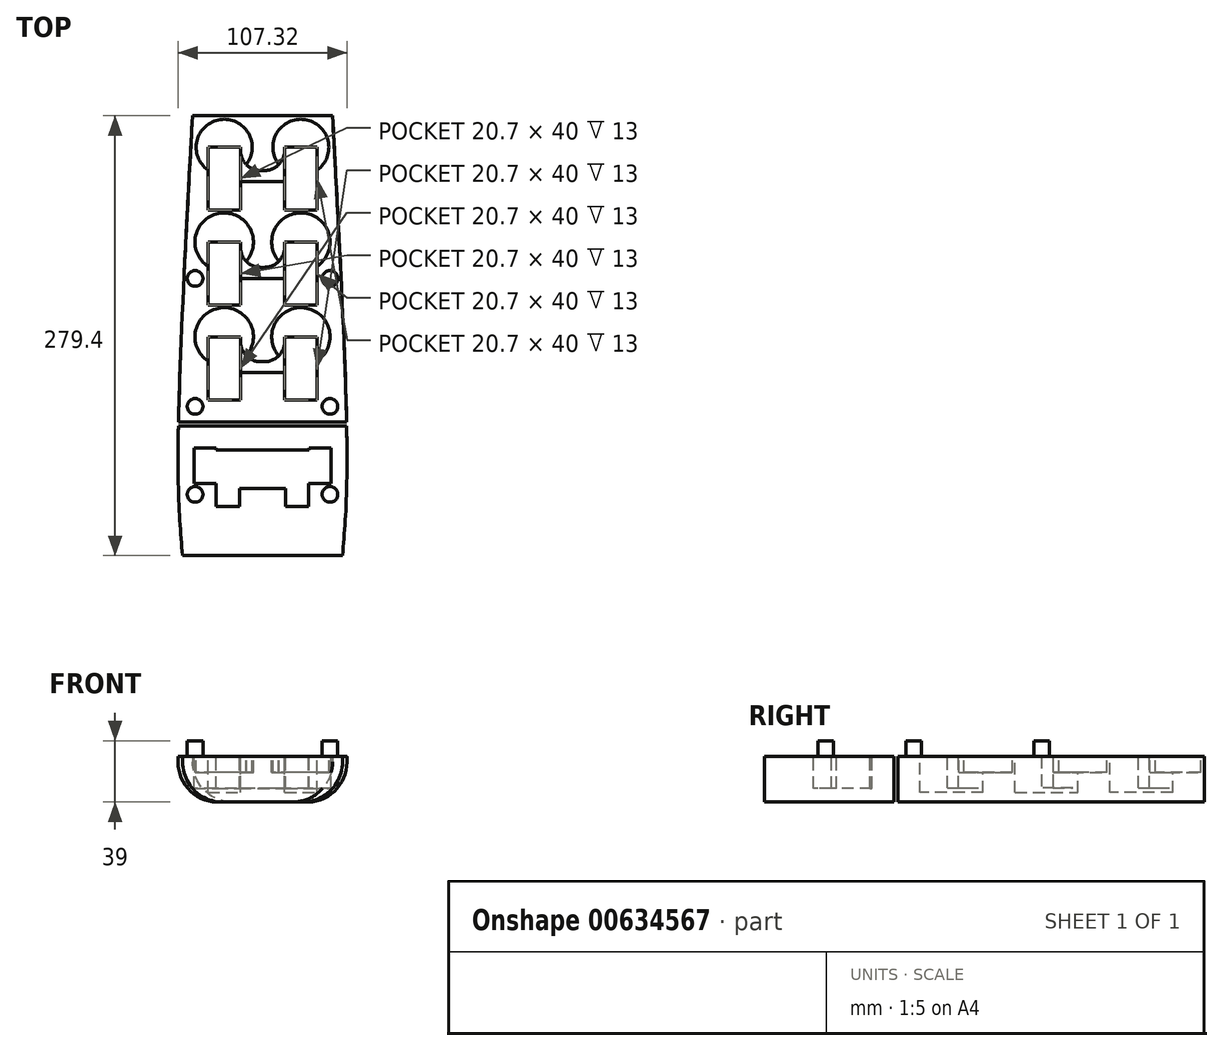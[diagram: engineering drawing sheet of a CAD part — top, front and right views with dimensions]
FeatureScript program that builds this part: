
annotation { "Feature Type Name" : "Feature", "Feature Type Description" : "" }
export const myFeature = defineFeature(function(context is Context, id is Id, definition is map)
    precondition{}
    {
        {
            var Q0;
            Q0=qCreatedBy(makeId("Top.planeOp"),FACE);
            var sketch = newSketch(context, id + "F0", { "sketchPlane" : qUnion([Q0])});
            skLineSegment(sketch, "E0", {"start": v(-44.45, 139.7) * mm, "end": v(44.45, 139.7) * mm});
            skLineSegment(sketch, "E1", {"start": v(0, 139.7) * mm, "end": v(0, -139.7) * mm, "construction": true});
            skLineSegment(sketch, "E2", {"start": v(0, -139.7) * mm, "end": v(-50.8, -139.7) * mm});
            skFitSpline(sketch, "E3", {"points": [v(-44.45, 139.7) * mm, v(-53.65, -82.07) * mm, v(-50.8, -139.7) * mm], "startDerivative": vector(-21.3, -389.22) * mm, "endDerivative": vector(12.22, -142.93) * mm});
            skFitSpline(sketch, "E4.MirrorCS", {"points": [v(44.45, 139.7) * mm, v(53.65, -82.07) * mm, v(50.8, -139.7) * mm], "startDerivative": vector(21.3, -389.22) * mm, "endDerivative": vector(-12.22, -142.93) * mm});
            skLineSegment(sketch, "E5.MirrorCS", {"start": v(0, -139.7) * mm, "end": v(50.8, -139.7) * mm});
            skSolve(sketch);
        }
        {
            var Q0;
            Q0=qSketchRegion(id+"F0",true);
            extrude(context, id + "F1", {"entities" : qUnion([Q0]), "depth" : 29 * mm, "offsetDistance" : 25.4 * mm});
        }
        {
            var Q0;
            Q0=makeQuery(id+"F1.opExtrude","CAP_EDGE",EDGE,{"disambiguationData":[OSD([sQuery(id+"F0.wireOp",EDGE,"E3")])],"isStart":true});
            var Q1;
            Q1=makeQuery(id+"F1.opExtrude","CAP_EDGE",EDGE,{"disambiguationData":[OSD([sQuery(id+"F0.wireOp",EDGE,"E4.MirrorCS")])],"isStart":true});
            fillet(context, id + "F2", {"entities" : qUnion([Q0, Q1]), "radius" : 25.4 * mm, "tangentPropagation" : true, "allowEdgeOverflow" : false});
        }
        {
            var Q0;
            Q0=makeQuery(id+"F1.opExtrude","CAP_FACE",FACE,{"disambiguationData":[OSD([sQuery(id+"F0.wireOp",EDGE,"E0"),sQuery(id+"F0.wireOp",EDGE,"E2"),sQuery(id+"F0.wireOp",EDGE,"E3"),sQuery(id+"F0.wireOp",EDGE,"E4.MirrorCS"),sQuery(id+"F0.wireOp",EDGE,"E5.MirrorCS")])],"isStart":false});
            var sketch = newSketch(context, id + "F3", { "sketchPlane" : qUnion([Q0])});
            skLineSegment(sketch, "E6.bottom", {"start": v(-34.7, 119.7) * mm, "end": v(-14, 119.7) * mm});
            skLineSegment(sketch, "E6.top", {"start": v(-34.7, 79.7) * mm, "end": v(-14, 79.7) * mm});
            skLineSegment(sketch, "E6.left", {"start": v(-34.7, 119.7) * mm, "end": v(-34.7, 79.7) * mm});
            skLineSegment(sketch, "E6.right", {"start": v(-14, 119.7) * mm, "end": v(-14, 79.7) * mm});
            skLineSegment(sketch, "E7", {"start": v(0, 139.7) * mm, "end": v(0, 0) * mm, "construction": true});
            skLineSegment(sketch, "E8", {"start": v(-38, 69.6) * mm, "end": v(36.85, 69.6) * mm, "construction": true});
            skLineSegment(sketch, "E9.MirrorCS", {"start": v(34.7, 119.7) * mm, "end": v(34.7, 79.7) * mm});
            skLineSegment(sketch, "E10.MirrorCS", {"start": v(14, 119.7) * mm, "end": v(14, 79.7) * mm});
            skLineSegment(sketch, "E11.MirrorCS", {"start": v(34.7, 79.7) * mm, "end": v(14, 79.7) * mm});
            skLineSegment(sketch, "E12.MirrorCS", {"start": v(34.7, 119.7) * mm, "end": v(14, 119.7) * mm});
            skLineSegment(sketch, "E13.MirrorCS", {"start": v(34.7, 19.5) * mm, "end": v(34.7, 59.5) * mm});
            skLineSegment(sketch, "E14.MirrorCS", {"start": v(-14, 19.5) * mm, "end": v(-14, 59.5) * mm});
            skLineSegment(sketch, "E15.MirrorCS", {"start": v(-34.7, 19.5) * mm, "end": v(-34.7, 59.5) * mm});
            skLineSegment(sketch, "E16.MirrorCS", {"start": v(-34.7, 59.5) * mm, "end": v(-14, 59.5) * mm});
            skLineSegment(sketch, "E17.MirrorCS", {"start": v(14, 19.5) * mm, "end": v(14, 59.5) * mm});
            skLineSegment(sketch, "E18.MirrorCS", {"start": v(34.7, 59.5) * mm, "end": v(14, 59.5) * mm});
            skLineSegment(sketch, "E19", {"start": v(-34.7, 19.5) * mm, "end": v(-14, 19.5) * mm});
            skLineSegment(sketch, "E20", {"start": v(14, 19.5) * mm, "end": v(34.7, 19.5) * mm});
            skLineSegment(sketch, "E21", {"start": v(-32.28, 9.4) * mm, "end": v(34.83, 9.4) * mm, "construction": true});
            skLineSegment(sketch, "E22.MirrorCS", {"start": v(-34.7, -40.7) * mm, "end": v(-14, -40.7) * mm});
            skLineSegment(sketch, "E23.MirrorCS", {"start": v(-34.7, -0.7) * mm, "end": v(-14, -0.7) * mm});
            skLineSegment(sketch, "E24.MirrorCS", {"start": v(34.7, -40.7) * mm, "end": v(14, -40.7) * mm});
            skLineSegment(sketch, "E25.MirrorCS", {"start": v(14, -0.7) * mm, "end": v(34.7, -0.7) * mm});
            skLineSegment(sketch, "E26.MirrorCS", {"start": v(-34.7, -0.7) * mm, "end": v(-34.7, -40.7) * mm});
            skLineSegment(sketch, "E27.MirrorCS", {"start": v(-14, -0.7) * mm, "end": v(-14, -40.7) * mm});
            skLineSegment(sketch, "E28.MirrorCS", {"start": v(34.7, -0.7) * mm, "end": v(34.7, -40.7) * mm});
            skLineSegment(sketch, "E29.MirrorCS", {"start": v(14, -0.7) * mm, "end": v(14, -40.7) * mm});
            skSolve(sketch);
        }
        {
            var Q0;
            Q0=qSketchRegion(id+"F3",true);
            extrude(context, id + "F4", {"entities" : qUnion([Q0]), "operationType" : NewBodyOperationType.REMOVE, "oppositeDirection" : true, "depth" : 23 * mm, "offsetDistance" : 25.4 * mm});
        }
        {
            var Q0;
            Q0=makeQuery(id+"F1.opExtrude","CAP_FACE",FACE,{"disambiguationData":[OSD([sQuery(id+"F0.wireOp",EDGE,"E0"),sQuery(id+"F0.wireOp",EDGE,"E2"),sQuery(id+"F0.wireOp",EDGE,"E3"),sQuery(id+"F0.wireOp",EDGE,"E4.MirrorCS"),sQuery(id+"F0.wireOp",EDGE,"E5.MirrorCS")])],"isStart":false});
            var sketch = newSketch(context, id + "F5", { "sketchPlane" : qUnion([Q0])});
            skCircle(sketch, "E30", {"center": v(-24.35, 119.7) * mm, "radius": 17.78 * mm});
            skCircle(sketch, "E31", {"center": v(24.35, 119.7) * mm, "radius": 17.78 * mm});
            skCircle(sketch, "E32", {"center": v(-24.35, 59.5) * mm, "radius": 18.54 * mm});
            skCircle(sketch, "E33", {"center": v(24.35, 59.5) * mm, "radius": 18.54 * mm});
            skCircle(sketch, "E34", {"center": v(-24.35, -0.7) * mm, "radius": 18.54 * mm});
            skCircle(sketch, "E35", {"center": v(24.35, -0.7) * mm, "radius": 18.54 * mm});
            skSolve(sketch);
        }
        {
            var Q0;
            Q0=qSketchRegion(id+"F5",true);
            extrude(context, id + "F6", {"entities" : qUnion([Q0]), "operationType" : NewBodyOperationType.REMOVE, "oppositeDirection" : true, "depth" : 10 * mm, "offsetDistance" : 25.4 * mm});
        }
        {
            var Q0;
            Q0=makeQuery(id+"F1.opExtrude","CAP_FACE",FACE,{"disambiguationData":[OSD([sQuery(id+"F0.wireOp",EDGE,"E0"),sQuery(id+"F0.wireOp",EDGE,"E2"),sQuery(id+"F0.wireOp",EDGE,"E3"),sQuery(id+"F0.wireOp",EDGE,"E4.MirrorCS"),sQuery(id+"F0.wireOp",EDGE,"E5.MirrorCS")])],"isStart":false});
            var sketch = newSketch(context, id + "F7", { "sketchPlane" : qUnion([Q0])});
            skSolve(sketch);
        }
        {
            var Q0;
            Q0=makeQuery(id+"F7.imprint","IMPRINT",FACE,{"disambiguationData":[TD([[makeQuery(id+"F7.imprint","IMPRINT",EDGE,{"derivedFrom":makeQuery(id+"F1.opExtrude","CAP_EDGE",EDGE,{"disambiguationData":[OSD([sQuery(id+"F0.wireOp",EDGE,"E0")])],"isStart":false})}),-1.0]])]});
            var sketch = newSketch(context, id + "F8", { "sketchPlane" : qUnion([Q0])});
            skLineSegment(sketch, "E36.bottom", {"start": v(-22.32, -16.47) * mm, "end": v(25.6, -16.47) * mm});
            skLineSegment(sketch, "E36.top", {"start": v(-22.32, -23.47) * mm, "end": v(25.6, -23.47) * mm});
            skLineSegment(sketch, "E36.left", {"start": v(-22.32, -16.47) * mm, "end": v(-22.32, -23.47) * mm});
            skLineSegment(sketch, "E36.right", {"start": v(25.6, -16.47) * mm, "end": v(25.6, -23.47) * mm});
            skLineSegment(sketch, "E37.bottom", {"start": v(-25.01, 43.48) * mm, "end": v(25.6, 43.48) * mm});
            skLineSegment(sketch, "E37.top", {"start": v(-25.01, 36.48) * mm, "end": v(25.6, 36.48) * mm});
            skLineSegment(sketch, "E37.left", {"start": v(-25.01, 43.48) * mm, "end": v(-25.01, 36.48) * mm});
            skLineSegment(sketch, "E37.right", {"start": v(25.6, 43.48) * mm, "end": v(25.6, 36.48) * mm});
            skLineSegment(sketch, "E38.bottom", {"start": v(-26.09, 104.99) * mm, "end": v(25.6, 104.99) * mm});
            skLineSegment(sketch, "E38.top", {"start": v(-26.09, 97.99) * mm, "end": v(25.6, 97.99) * mm});
            skLineSegment(sketch, "E38.left", {"start": v(-26.09, 104.99) * mm, "end": v(-26.09, 97.99) * mm});
            skLineSegment(sketch, "E38.right", {"start": v(25.6, 104.99) * mm, "end": v(25.6, 97.99) * mm});
            skSolve(sketch);
        }
        {
            var Q0;
            Q0=qSketchRegion(id+"F8",true);
            extrude(context, id + "F9", {"entities" : qUnion([Q0]), "operationType" : NewBodyOperationType.REMOVE, "oppositeDirection" : true, "depth" : 20 * mm, "offsetDistance" : 25.4 * mm});
        }
        {
            var Q0;
            Q0=makeQuery(id+"F9.boolean.opBoolean","INTERSECT",EDGE,{"derivedFrom":[makeQuery(id+"F4.boolean.opBoolean","COPY",FACE,{"derivedFrom":makeQuery(id+"F4.opExtrude","SWEPT_FACE",FACE,{"disambiguationData":[OSD([sQuery(id+"F3.wireOp",EDGE,"E6.right")])]})}),makeQuery(id+"F9.opExtrude","SWEPT_FACE",FACE,{"disambiguationData":[OSD([sQuery(id+"F8.wireOp",EDGE,"E38.bottom")])]})]});
            var Q1;
            Q1=makeQuery(id+"F9.boolean.opBoolean","INTERSECT",EDGE,{"derivedFrom":[makeQuery(id+"F4.boolean.opBoolean","COPY",FACE,{"derivedFrom":makeQuery(id+"F4.opExtrude","SWEPT_FACE",FACE,{"disambiguationData":[OSD([sQuery(id+"F3.wireOp",EDGE,"E10.MirrorCS")])]})}),makeQuery(id+"F9.opExtrude","SWEPT_FACE",FACE,{"disambiguationData":[OSD([sQuery(id+"F8.wireOp",EDGE,"E38.bottom")])]})]});
            var Q2;
            Q2=makeQuery(id+"F9.boolean.opBoolean","INTERSECT",EDGE,{"derivedFrom":[makeQuery(id+"F4.boolean.opBoolean","COPY",FACE,{"derivedFrom":makeQuery(id+"F4.opExtrude","SWEPT_FACE",FACE,{"disambiguationData":[OSD([sQuery(id+"F3.wireOp",EDGE,"E17.MirrorCS")])]})}),makeQuery(id+"F9.opExtrude","SWEPT_FACE",FACE,{"disambiguationData":[OSD([sQuery(id+"F8.wireOp",EDGE,"E37.bottom")])]})]});
            var Q3;
            Q3=makeQuery(id+"F9.boolean.opBoolean","INTERSECT",EDGE,{"derivedFrom":[makeQuery(id+"F4.boolean.opBoolean","COPY",FACE,{"derivedFrom":makeQuery(id+"F4.opExtrude","SWEPT_FACE",FACE,{"disambiguationData":[OSD([sQuery(id+"F3.wireOp",EDGE,"E14.MirrorCS")])]})}),makeQuery(id+"F9.opExtrude","SWEPT_FACE",FACE,{"disambiguationData":[OSD([sQuery(id+"F8.wireOp",EDGE,"E37.bottom")])]})]});
            var Q4;
            Q4=makeQuery(id+"F9.boolean.opBoolean","INTERSECT",EDGE,{"derivedFrom":[makeQuery(id+"F4.boolean.opBoolean","COPY",FACE,{"derivedFrom":makeQuery(id+"F4.opExtrude","SWEPT_FACE",FACE,{"disambiguationData":[OSD([sQuery(id+"F3.wireOp",EDGE,"E27.MirrorCS")])]})}),makeQuery(id+"F9.opExtrude","SWEPT_FACE",FACE,{"disambiguationData":[OSD([sQuery(id+"F8.wireOp",EDGE,"E36.bottom")])]})]});
            var Q5;
            Q5=makeQuery(id+"F9.boolean.opBoolean","INTERSECT",EDGE,{"derivedFrom":[makeQuery(id+"F4.boolean.opBoolean","COPY",FACE,{"derivedFrom":makeQuery(id+"F4.opExtrude","SWEPT_FACE",FACE,{"disambiguationData":[OSD([sQuery(id+"F3.wireOp",EDGE,"E29.MirrorCS")])]})}),makeQuery(id+"F9.opExtrude","SWEPT_FACE",FACE,{"disambiguationData":[OSD([sQuery(id+"F8.wireOp",EDGE,"E36.bottom")])]})]});
            fillet(context, id + "F10", {"entities" : qUnion([Q0, Q1, Q2, Q3, Q4, Q5]), "radius" : 12.7 * mm, "tangentPropagation" : true, "allowEdgeOverflow" : false});
        }
        {
            var Q0;
            Q0=makeQuery(id+"F7.imprint","IMPRINT",FACE,{"disambiguationData":[TD([[makeQuery(id+"F7.imprint","IMPRINT",EDGE,{"derivedFrom":makeQuery(id+"F1.opExtrude","CAP_EDGE",EDGE,{"disambiguationData":[OSD([sQuery(id+"F0.wireOp",EDGE,"E0")])],"isStart":false})}),-1.0]])]});
            var sketch = newSketch(context, id + "F11", { "sketchPlane" : qUnion([Q0])});
            skLineSegment(sketch, "E39.bottom", {"start": v(-65.32, -54.88) * mm, "end": v(72.26, -54.88) * mm});
            skLineSegment(sketch, "E39.top", {"start": v(-65.32, -57.24) * mm, "end": v(72.26, -57.24) * mm});
            skLineSegment(sketch, "E39.left", {"start": v(-65.32, -54.88) * mm, "end": v(-65.32, -57.24) * mm});
            skLineSegment(sketch, "E39.right", {"start": v(72.26, -54.88) * mm, "end": v(72.26, -57.24) * mm});
            skSolve(sketch);
        }
        {
            var Q0;
            Q0=qSketchRegion(id+"F11",true);
            extrude(context, id + "F12", {"entities" : qUnion([Q0]), "operationType" : NewBodyOperationType.REMOVE, "oppositeDirection" : true, "depth" : 508 * mm, "offsetDistance" : 25.4 * mm});
        }
        {
            var Q0;
            Q0=makeQuery(id+"F7.imprint","IMPRINT",FACE,{"disambiguationData":[TD([[makeQuery(id+"F7.imprint","IMPRINT",EDGE,{"derivedFrom":makeQuery(id+"F1.opExtrude","CAP_EDGE",EDGE,{"disambiguationData":[OSD([sQuery(id+"F0.wireOp",EDGE,"E0")])],"isStart":false})}),-1.0]])]});
            var sketch = newSketch(context, id + "F13", { "sketchPlane" : qUnion([Q0])});
            skCircle(sketch, "E40", {"center": v(-42.83, -44.88) * mm, "radius": 4.95 * mm});
            skLineSegment(sketch, "E41", {"start": v(0, 30.1) * mm, "end": v(0, -70.05) * mm, "construction": true});
            skLineSegment(sketch, "E42", {"start": v(-82.32, -4.24) * mm, "end": v(87.3, -4.24) * mm, "construction": true});
            skCircle(sketch, "E43.MirrorC", {"center": v(42.83, -44.88) * mm, "radius": 4.95 * mm});
            skCircle(sketch, "E44.MirrorC", {"center": v(-42.83, 36.4) * mm, "radius": 4.95 * mm});
            skCircle(sketch, "E45.MirrorC", {"center": v(42.83, 36.4) * mm, "radius": 4.95 * mm});
            skLineSegment(sketch, "E46", {"start": v(-86.45, -72.82) * mm, "end": v(91.93, -72.82) * mm, "construction": true});
            skCircle(sketch, "E47.MirrorC", {"center": v(-42.83, -100.76) * mm, "radius": 4.95 * mm});
            skCircle(sketch, "E48.MirrorC", {"center": v(42.83, -100.76) * mm, "radius": 4.95 * mm});
            skSolve(sketch);
        }
        {
            var Q0;
            Q0=qSketchRegion(id+"F13",true);
            extrude(context, id + "F14", {"entities" : qUnion([Q0]), "operationType" : NewBodyOperationType.ADD, "depth" : 10 * mm, "offsetDistance" : 25.4 * mm});
        }
        {
            var Q0;
            Q0=makeQuery(id+"F7.imprint","IMPRINT",FACE,{"disambiguationData":[TD([[makeQuery(id+"F7.imprint","IMPRINT",EDGE,{"derivedFrom":makeQuery(id+"F1.opExtrude","CAP_EDGE",EDGE,{"disambiguationData":[OSD([sQuery(id+"F0.wireOp",EDGE,"E0")])],"isStart":false})}),-1.0]])]});
            var sketch = newSketch(context, id + "F15", { "sketchPlane" : qUnion([Q0])});
            skLineSegment(sketch, "E49", {"start": v(0, 0) * mm, "end": v(0, -126.7) * mm, "construction": true});
            skLineSegment(sketch, "E50", {"start": v(42.6, -57.24) * mm, "end": v(-44.07, -57.24) * mm, "construction": true});
            skLineSegment(sketch, "E51", {"start": v(0, 4.55) * mm, "end": v(0, -51.7) * mm, "construction": true});
            skLineSegment(sketch, "E52.top", {"start": v(-14.62, -97.03) * mm, "end": v(0, -97.03) * mm});
            skLineSegment(sketch, "E52.right", {"start": v(0, -27.56) * mm, "end": v(0, -97.03) * mm});
            skLineSegment(sketch, "E53.bottom", {"start": v(-29.62, -79.23) * mm, "end": v(-14.62, -79.23) * mm});
            skLineSegment(sketch, "E53.top", {"start": v(-29.62, -84.55) * mm, "end": v(-29.48, -84.55) * mm});
            skLineSegment(sketch, "E53.left", {"start": v(-29.62, -79.23) * mm, "end": v(-29.62, -84.55) * mm});
            skLineSegment(sketch, "E53.right", {"start": v(-14.62, -79.23) * mm, "end": v(-14.62, -84.55) * mm});
            skLineSegment(sketch, "E54.bottom", {"start": v(-29.62, -79.23) * mm, "end": v(0, -79.23) * mm});
            skLineSegment(sketch, "E54.top", {"start": v(-29.62, -72.47) * mm, "end": v(0, -72.47) * mm});
            skLineSegment(sketch, "E54.left", {"start": v(-29.62, -79.23) * mm, "end": v(-29.62, -72.47) * mm});
            skLineSegment(sketch, "E54.right", {"start": v(0, -79.23) * mm, "end": v(0, -72.47) * mm});
            skLineSegment(sketch, "E55.bottom", {"start": v(0, -97.03) * mm, "end": v(0, -97.03) * mm});
            skLineSegment(sketch, "E55.top", {"start": v(0, -72.47) * mm, "end": v(0, -72.47) * mm});
            skLineSegment(sketch, "E55.left", {"start": v(0, -97.03) * mm, "end": v(0, -72.47) * mm});
            skLineSegment(sketch, "E55.right", {"start": v(0, -97.03) * mm, "end": v(0, -72.47) * mm});
            skLineSegment(sketch, "E56.bottom", {"start": v(-29.62, -84.55) * mm, "end": v(-43.57, -84.55) * mm});
            skLineSegment(sketch, "E56.top", {"start": v(-29.62, -71.42) * mm, "end": v(-43.57, -71.42) * mm});
            skLineSegment(sketch, "E56.left", {"start": v(-29.62, -84.55) * mm, "end": v(-29.62, -71.42) * mm});
            skLineSegment(sketch, "E56.right", {"start": v(-43.57, -84.55) * mm, "end": v(-43.57, -71.42) * mm});
            skLineSegment(sketch, "E57.MirrorCS", {"start": v(29.62, -84.55) * mm, "end": v(29.62, -71.42) * mm});
            skLineSegment(sketch, "E58.MirrorCS", {"start": v(29.62, -84.55) * mm, "end": v(43.57, -84.55) * mm});
            skLineSegment(sketch, "E59.MirrorCS", {"start": v(29.62, -79.23) * mm, "end": v(14.62, -79.23) * mm});
            skLineSegment(sketch, "E60.MirrorCS", {"start": v(43.57, -84.55) * mm, "end": v(43.57, -71.42) * mm});
            skLineSegment(sketch, "E61.MirrorCS", {"start": v(29.62, -84.55) * mm, "end": v(29.28, -84.55) * mm});
            skLineSegment(sketch, "E62.MirrorCS", {"start": v(29.62, -79.23) * mm, "end": v(29.62, -84.55) * mm});
            skLineSegment(sketch, "E63.MirrorCS", {"start": v(14.62, -79.23) * mm, "end": v(14.62, -84.55) * mm});
            skLineSegment(sketch, "E64.MirrorCS", {"start": v(29.62, -71.42) * mm, "end": v(43.57, -71.42) * mm});
            skLineSegment(sketch, "E65.MirrorCS", {"start": v(29.62, -79.23) * mm, "end": v(29.62, -72.47) * mm});
            skLineSegment(sketch, "E66.MirrorCS", {"start": v(14.62, -97.03) * mm, "end": v(0, -97.03) * mm});
            skLineSegment(sketch, "E67.MirrorCS", {"start": v(29.62, -72.47) * mm, "end": v(0, -72.47) * mm});
            skLineSegment(sketch, "E68", {"start": v(-14.62, -97.03) * mm, "end": v(-14.62, -84.55) * mm});
            skLineSegment(sketch, "E69", {"start": v(14.62, -97.03) * mm, "end": v(14.62, -84.55) * mm});
            skLineSegment(sketch, "E70.bottom", {"start": v(-43.57, -84.55) * mm, "end": v(-29.48, -84.55) * mm});
            skLineSegment(sketch, "E70.top", {"start": v(-43.57, -93.94) * mm, "end": v(-29.48, -93.94) * mm});
            skLineSegment(sketch, "E70.left", {"start": v(-43.57, -84.55) * mm, "end": v(-43.57, -93.94) * mm});
            skLineSegment(sketch, "E70.right", {"start": v(-29.48, -84.55) * mm, "end": v(-29.48, -93.94) * mm});
            skLineSegment(sketch, "E71.bottom", {"start": v(43.57, -84.55) * mm, "end": v(29.28, -84.55) * mm});
            skLineSegment(sketch, "E71.top", {"start": v(43.57, -93.94) * mm, "end": v(29.28, -93.94) * mm});
            skLineSegment(sketch, "E71.left", {"start": v(43.57, -84.55) * mm, "end": v(43.57, -93.94) * mm});
            skLineSegment(sketch, "E71.right", {"start": v(29.28, -84.55) * mm, "end": v(29.28, -93.94) * mm});
            skLineSegment(sketch, "E72.top", {"start": v(-29.48, -97.03) * mm, "end": v(-14.62, -97.03) * mm});
            skLineSegment(sketch, "E72.left", {"start": v(-29.48, -84.55) * mm, "end": v(-29.48, -97.03) * mm});
            skLineSegment(sketch, "E72.right", {"start": v(-14.62, -84.55) * mm, "end": v(-14.62, -97.03) * mm});
            skLineSegment(sketch, "E73.top", {"start": v(-29.48, -108.46) * mm, "end": v(-14.62, -108.46) * mm});
            skLineSegment(sketch, "E73.left", {"start": v(-29.48, -97.03) * mm, "end": v(-29.48, -108.46) * mm});
            skLineSegment(sketch, "E73.right", {"start": v(-14.62, -97.03) * mm, "end": v(-14.62, -108.46) * mm});
            skLineSegment(sketch, "E74.top", {"start": v(29.28, -97.03) * mm, "end": v(14.62, -97.03) * mm});
            skLineSegment(sketch, "E74.left", {"start": v(29.28, -84.55) * mm, "end": v(29.28, -97.03) * mm});
            skLineSegment(sketch, "E74.right", {"start": v(14.62, -84.55) * mm, "end": v(14.62, -97.03) * mm});
            skLineSegment(sketch, "E75.bottom", {"start": v(14.62, -97.03) * mm, "end": v(29.32, -97.03) * mm});
            skLineSegment(sketch, "E75.top", {"start": v(14.62, -108.46) * mm, "end": v(29.32, -108.46) * mm});
            skLineSegment(sketch, "E75.left", {"start": v(14.62, -97.03) * mm, "end": v(14.62, -108.46) * mm});
            skLineSegment(sketch, "E75.right", {"start": v(29.32, -97.03) * mm, "end": v(29.32, -108.46) * mm});
            skLineSegment(sketch, "E76.bottom", {"start": v(14.62, -79.23) * mm, "end": v(29.62, -79.23) * mm});
            skLineSegment(sketch, "E76.top", {"start": v(29.28, -84.55) * mm, "end": v(29.62, -84.55) * mm});
            skSolve(sketch);
        }
        {
            var Q0;
            Q0=qSketchRegion(id+"F15",true);
            extrude(context, id + "F16", {"entities" : qUnion([Q0]), "operationType" : NewBodyOperationType.REMOVE, "oppositeDirection" : true, "depth" : 20.32 * mm, "offsetDistance" : 25.4 * mm});
        }
    });
